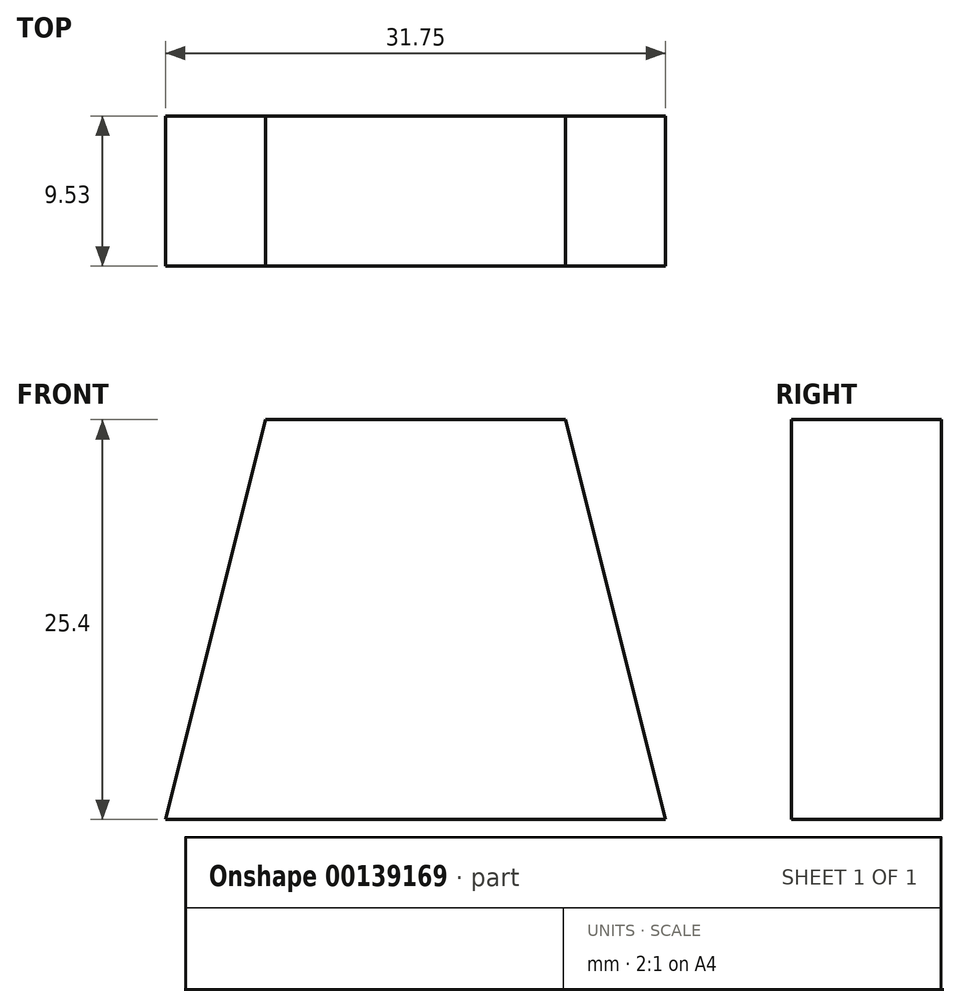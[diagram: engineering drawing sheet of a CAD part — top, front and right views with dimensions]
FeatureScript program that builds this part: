
annotation { "Feature Type Name" : "Feature", "Feature Type Description" : "" }
export const myFeature = defineFeature(function(context is Context, id is Id, definition is map)
    precondition{}
    {
        {
            var Q0;
            Q0=qCreatedBy(makeId("Front.planeOp"),FACE);
            var sketch = newSketch(context, id + "F0", { "sketchPlane" : qUnion([Q0])});
            skLineSegment(sketch, "E0", {"start": v(0, 25.4) * mm, "end": v(19.05, 25.4) * mm});
            skLineSegment(sketch, "E1", {"start": v(0, 0) * mm, "end": v(25.4, 0) * mm});
            skLineSegment(sketch, "E2", {"start": v(25.4, 0) * mm, "end": v(19.05, 25.4) * mm});
            skLineSegment(sketch, "E3", {"start": v(-6.35, 0) * mm, "end": v(0, 25.4) * mm});
            skLineSegment(sketch, "E4", {"start": v(0, 0) * mm, "end": v(-6.35, 0) * mm});
            skSolve(sketch);
        }
        {
            var Q0;
            Q0 = qSketchRegion(id + "F0", true);
            extrude(context, id + "F1", {"entities" : qUnion([Q0]), "depth" : 9.52 * mm});
        }
    });
